# Revit family: ElectricalEquipment_Hager_Design30_HighIntegrityDual
name_source: partatom
category: Electrical Equipment
revit_build: Autodesk Revit 2015 (Build: 20160512_1515(x64)
units: mm (PartAtom-declared; Revit-internal decimal feet)

## types (12) — shared parameters
Assembly Code = D5010
AssetType = Fixed
Category = ElectricalEquipment
ClassificationName = Uniclass2015
ClassificationValue = Pr_80_77_28_16
Colour = RAL9010WhiteGloss
Default Elevation = 500 mm  [stored 1.64042 ft]
DocumentationLiterature = http://www.hager.co.uk
DocumentationTechnical = http://www.hager.co.uk
DurationUnit = Years
ExpectedLife = 10
IfcExportAs = ElectricalEquipment
IfcExportType = ElectricalEquipment
Keynote = V
Mains Type = AC
Manufacturer = Hager
ManufacturerName = Hager
Material = MildSteel,ABS,AcousticComposite
NBSDescription = ElectricalEquipment
NBSReference = Pr_80_77_28_16
Neutral Rating = 100.00%
NominalDepth = 103 mm
NominalLength = 480 mm  [stored 1.5748 ft]
NominalWidth = 103 mm
Shape = Rectangular
URL = http://www.hager.co.uk
Voltage = 230V
WarrantyDescription = See Manufacturer
WarrantyDurationParts = 2
WarrantyDurationUnit = Years
WarrantyGuarantorParts = 2
_BimstoreBibleVersion = V14
_DistributedBy = www.bimstore.co.uk
zero-valued in all types: ReplacementCost, ServiceLifeDuration, WarrantyDurationLabor, _BimSpecGuid, _CurrentRevision

## per-type parameters (varying)
| type | A | B | BIMObjectName | C | Description | EAN | Features | NBSObjectName | NominalHeight | TypeName |
| VM70810CU | 137 mm  [stored 0.449475 ft] | 137 mm  [stored 0.449475 ft] | Hager_ElectricalEquipment_HighIntegrity_VM70810CU | 46 mm | DualRowHighIntegrity8+10Way100ASW2*63A30mARCCB | 3250610458679 | DualRowHighIntegrity8+10Way100ASW2*63A30mARCCB | Hager_HighIntegrity_VM70810CU | 293 mm  [stored 0.961286 ft] | ElectricalEquipment_HighIntegrity_VM70810CU |
| VM71214CU | 173 mm | 173 mm | Hager_ElectricalEquipment_HighIntegrity_VM71214CU | 58 mm | DualRowHighIntegrity12+14Way100ASW2*63A30mARCCB | 3250610458723 | DualRowHighIntegrity12+14Way100ASW2*63A30mARCCB | Hager_HighIntegrity_VM71214CU | 364 mm  [stored 1.19423 ft] | ElectricalEquipment_HighIntegrity_VM71214CU |
| VM71820CU | 227 mm | 227 mm | Hager_ElectricalEquipment_HighIntegrity_VM71820CU | 76 mm | DualRowHighIntegrity18+20Way100ASW2*63A30mARCCB | 3250610458785 | DualRowHighIntegrity18+20Way100ASW2*63A30mARCCB | Hager_HighIntegrity_VM71820CU | 472 mm | ElectricalEquipment_HighIntegrity_VM71214CU |
| VM80810CU | 137 mm  [stored 0.449475 ft] | 137 mm  [stored 0.449475 ft] | Hager_ElectricalEquipment_HighIntegrity_VM80810CU | 46 mm | DualRowHighIntegrity8+10Way100ASW2*80A30mARCCB | 3250610458853 | DualRowHighIntegrity8+10Way100ASW2*80A30mARCCB | Hager_HighIntegrity_VM80810CU | 293 mm  [stored 0.961286 ft] | ElectricalEquipment_HighIntegrity_VM80810CU |
| VM81214CU | 173 mm | 173 mm | Hager_ElectricalEquipment_HighIntegrity_VM81214CU | 58 mm | DualRowHighIntegrity12+14Way100ASW2*80A30mARCCB | 3250610458891 | DualRowHighIntegrity12+14Way100ASW2*80A30mARCCB | Hager_HighIntegrity_VM81214CU | 364 mm  [stored 1.19423 ft] | ElectricalEquipment_HighIntegrity_VM81214CU |
| VM81820CU | 227 mm | 227 mm | Hager_ElectricalEquipment_HighIntegrity_VM81820CU | 76 mm | DualRowHighIntegrity18+20Way100ASW2*80A30mARCCB | 3250610459041 | DualRowHighIntegrity18+20Way100ASW2*80A30mARCCB | Hager_HighIntegrity_VM81820CU | 472 mm | ElectricalEquipment_HighIntegrity_VM81214CU |
| VM70810CUK | 137 mm  [stored 0.449475 ft] | 137 mm  [stored 0.449475 ft] | Hager_ElectricalEquipment_HighIntegrity_VM70810CUK | 46 mm | DualRowHighIntegrity8+10Way100ASW2*80A30mARCCBKnockout | 3250610458686 | DualRowHighIntegrity8+10Way100ASW2*80A30mARCCBKnockout | Hager_HighIntegrity_VM70810CUK | 293 mm  [stored 0.961286 ft] | ElectricalEquipment_HighIntegrity_VM70810CUK |
| VM71214CUK | 173 mm | 173 mm | Hager_ElectricalEquipment_HighIntegrity_VM71214CUK | 58 mm | DualRowHighIntegrity12+14Way100ASW2*80A30mARCCBKnockout | 3250610458730 | DualRowHighIntegrity12+14Way100ASW2*80A30mARCCBKnockout | Hager_HighIntegrity_VM71214CUK | 364 mm  [stored 1.19423 ft] | ElectricalEquipment_HighIntegrity_VM71214CUK |
| VM71820CUK | 227 mm | 227 mm | Hager_ElectricalEquipment_HighIntegrity_VM71820CUK | 76 mm | DualRowHighIntegrity18+20Way100ASW2*80A30mARCCBKnockout | 3250610458792 | DualRowHighIntegrity18+20Way100ASW2*80A30mARCCBKnockout | Hager_HighIntegrity_VM71820CUK | 472 mm | ElectricalEquipment_HighIntegrity_VM71214CUK |
| VM80810CUK | 137 mm  [stored 0.449475 ft] | 137 mm  [stored 0.449475 ft] | Hager_ElectricalEquipment_HighIntegrity_VM80810CUK | 46 mm | DualRowHighIntegrity8+10Way100ASW2*80A30mARCCBKnockout | 3250610458860 | DualRowHighIntegrity8+10Way100ASW2*80A30mARCCBKnockout | Hager_HighIntegrity_VM80810CUK | 293 mm  [stored 0.961286 ft] | ElectricalEquipment_HighIntegrity_VM80810CUK |
| VM81214CUK | 173 mm | 173 mm | Hager_ElectricalEquipment_HighIntegrity_VM81214CUK | 58 mm | DualRowHighIntegrity12+14Way100ASW2*80A30mARCCBKnockout | 3250610458945 | DualRowHighIntegrity12+14Way100ASW2*80A30mARCCBKnockout | Hager_HighIntegrity_VM81214CUK | 364 mm  [stored 1.19423 ft] | ElectricalEquipment_HighIntegrity_VM81214CUK |
| VM81820CUK | 227 mm | 227 mm | Hager_ElectricalEquipment_HighIntegrity_VM81820CUK | 76 mm | DualRowHighIntegrity18+20Way100ASW2*80A30mARCCBKnockout | 3250610459058 | DualRowHighIntegrity18+20Way100ASW2*80A30mARCCBKnockout | Hager_HighIntegrity_VM81820CUK | 472 mm | ElectricalEquipment_HighIntegrity_VM81214CUK |

note: column(s) folded — value = type name in every type: Model, ModelNumber, ModelReference, Type Comments

note: [stored X ft] marks values corroborated as IEEE doubles in the binary element streams (Revit-internal decimal feet)

## geometry (parser evidence)
native form markers: Blend x2, Sweep x4
no freeform markers — native parametric forms only
